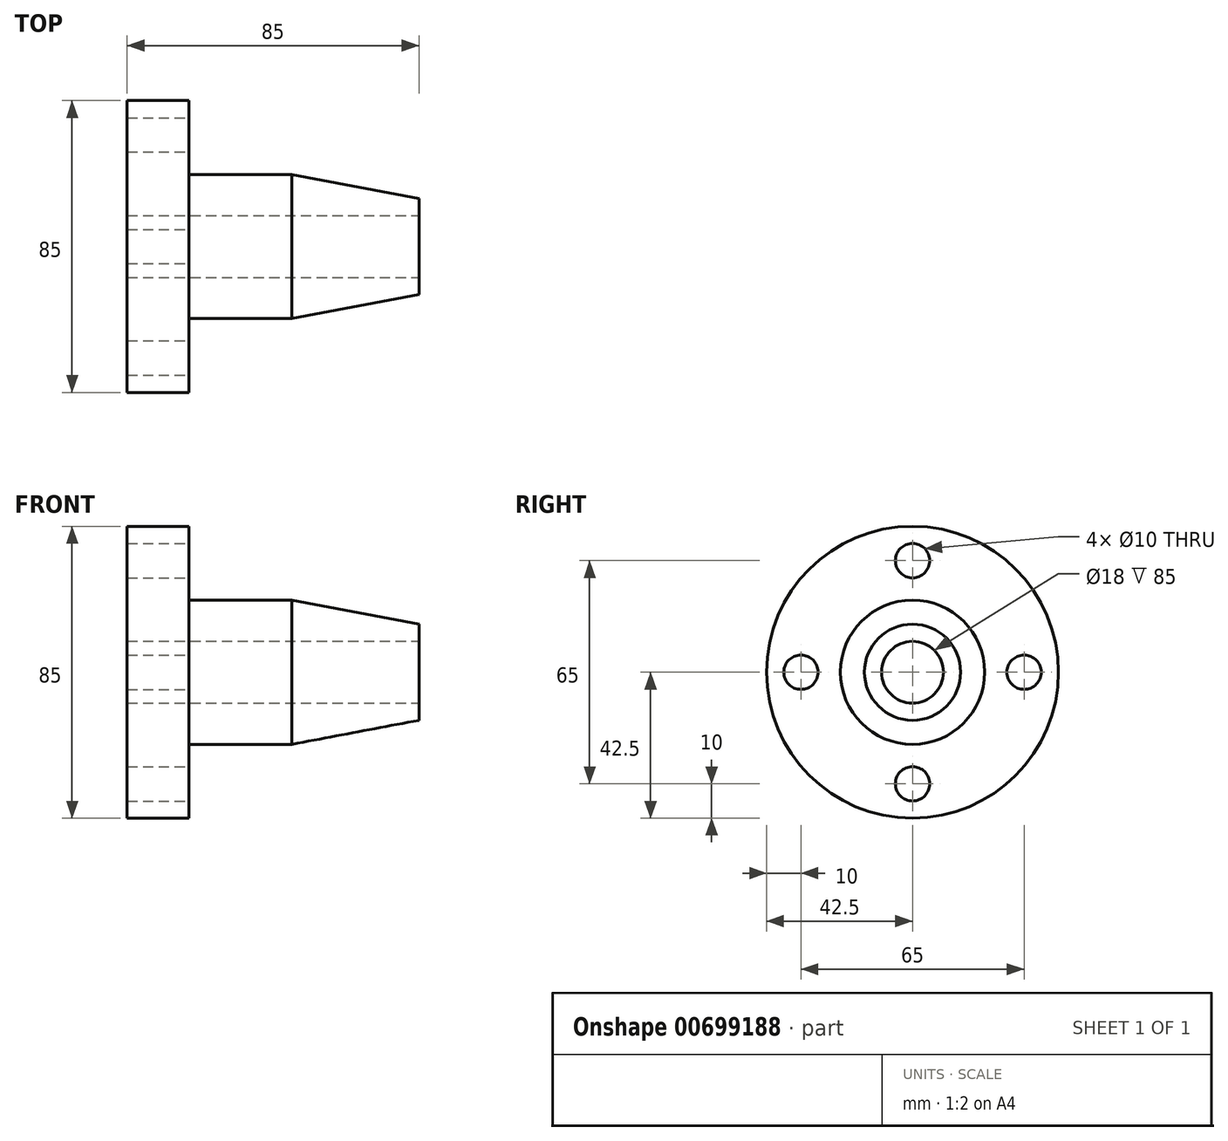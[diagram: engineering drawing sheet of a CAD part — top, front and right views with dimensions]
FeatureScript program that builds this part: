
annotation { "Feature Type Name" : "Feature", "Feature Type Description" : "" }
export const myFeature = defineFeature(function(context is Context, id is Id, definition is map)
    precondition{}
    {
        {
            var Q0;
            Q0=qCreatedBy(makeId("Top.planeOp"),FACE);
            var sketch = newSketch(context, id + "F0", { "sketchPlane" : qUnion([Q0])});
            skLineSegment(sketch, "E0", {"start": v(0, 9) * mm, "end": v(85, 9) * mm});
            skLineSegment(sketch, "E1", {"start": v(0, 0) * mm, "end": v(138.53, 0) * mm, "construction": true});
            skLineSegment(sketch, "E2", {"start": v(0, 9) * mm, "end": v(0, 42.5) * mm});
            skLineSegment(sketch, "E3", {"start": v(0, 42.5) * mm, "end": v(18, 42.5) * mm});
            skLineSegment(sketch, "E4", {"start": v(18, 42.5) * mm, "end": v(18, 21) * mm});
            skLineSegment(sketch, "E5", {"start": v(18, 21) * mm, "end": v(48, 21) * mm});
            skLineSegment(sketch, "E6", {"start": v(48, 21) * mm, "end": v(85, 14) * mm});
            skLineSegment(sketch, "E7", {"start": v(85, 14) * mm, "end": v(85, 9) * mm});
            skSolve(sketch);
        }
        {
            var Q0;
            Q0=makeQuery(id+"F0.imprint","IMPRINT",FACE,{"disambiguationData":[TD([[makeQuery(id+"F0.imprint","IMPRINT",EDGE,{"derivedFrom":sQuery(id+"F0.wireOp",EDGE,"E0")}),1.0]])]});
            var Q1;
            Q1=sQuery(id+"F0.wireOp",EDGE,"E1");
            revolve(context, id + "F1", {"entities" : qUnion([Q0]), "axis" : qUnion([Q1]), "revolveType" : RevolveType.FULL, "oppositeDirection" : true});
        }
        {
            var Q0;
            Q0=makeQuery(id+"F1.opRevolve","SWEPT_FACE",FACE,{"disambiguationData":[OSD([sQuery(id+"F0.wireOp",EDGE,"E4")])]});
            var sketch = newSketch(context, id + "F2", { "sketchPlane" : qUnion([Q0])});
            skCircle(sketch, "E8", {"center": v(0, 0) * mm, "radius": 32.5 * mm, "construction": true});
            skCircle(sketch, "E9", {"center": v(32.5, 0) * mm, "radius": 5 * mm});
            skCircle(sketch, "E10", {"center": v(0, 32.5) * mm, "radius": 5 * mm});
            skCircle(sketch, "E11", {"center": v(-32.5, 0) * mm, "radius": 5 * mm});
            skCircle(sketch, "E12", {"center": v(0, -32.5) * mm, "radius": 5 * mm});
            skSolve(sketch);
        }
        {
            var Q0;
            Q0=sQuery(id+"F2.wireOp",VERTEX,"E10.center");
            var Q1;
            Q1=sQuery(id+"F2.wireOp",VERTEX,"E11.center");
            var Q2;
            Q2=sQuery(id+"F2.wireOp",VERTEX,"E12.center");
            var Q3;
            Q3=sQuery(id+"F2.wireOp",VERTEX,"E9.center");
            var Q4;
            Q4=makeQuery(id+"F1.opRevolve","SWEPT_BODY",BODY,{"disambiguationData":[OSD([sQuery(id+"F0.wireOp",EDGE,"E0"),sQuery(id+"F0.wireOp",EDGE,"E2"),sQuery(id+"F0.wireOp",EDGE,"E3"),sQuery(id+"F0.wireOp",EDGE,"E4"),sQuery(id+"F0.wireOp",EDGE,"E5"),sQuery(id+"F0.wireOp",EDGE,"E6"),sQuery(id+"F0.wireOp",EDGE,"E7")])]});
            hole(context, id + "F3", {"style" : HoleStyle.SIMPLE, "endStyle" : HoleEndStyle.BLIND, "holeDiameter" : 10 * mm, "majorDiameter" : 5 * mm, "holeDepth" : 18 * mm, "isTappedThrough" : true, "tappedDepth" : 12 * mm, "tapClearance" : 3, "locations" : qUnion([Q0, Q1, Q2, Q3]), "scope" : qUnion([Q4])});
        }
    });
